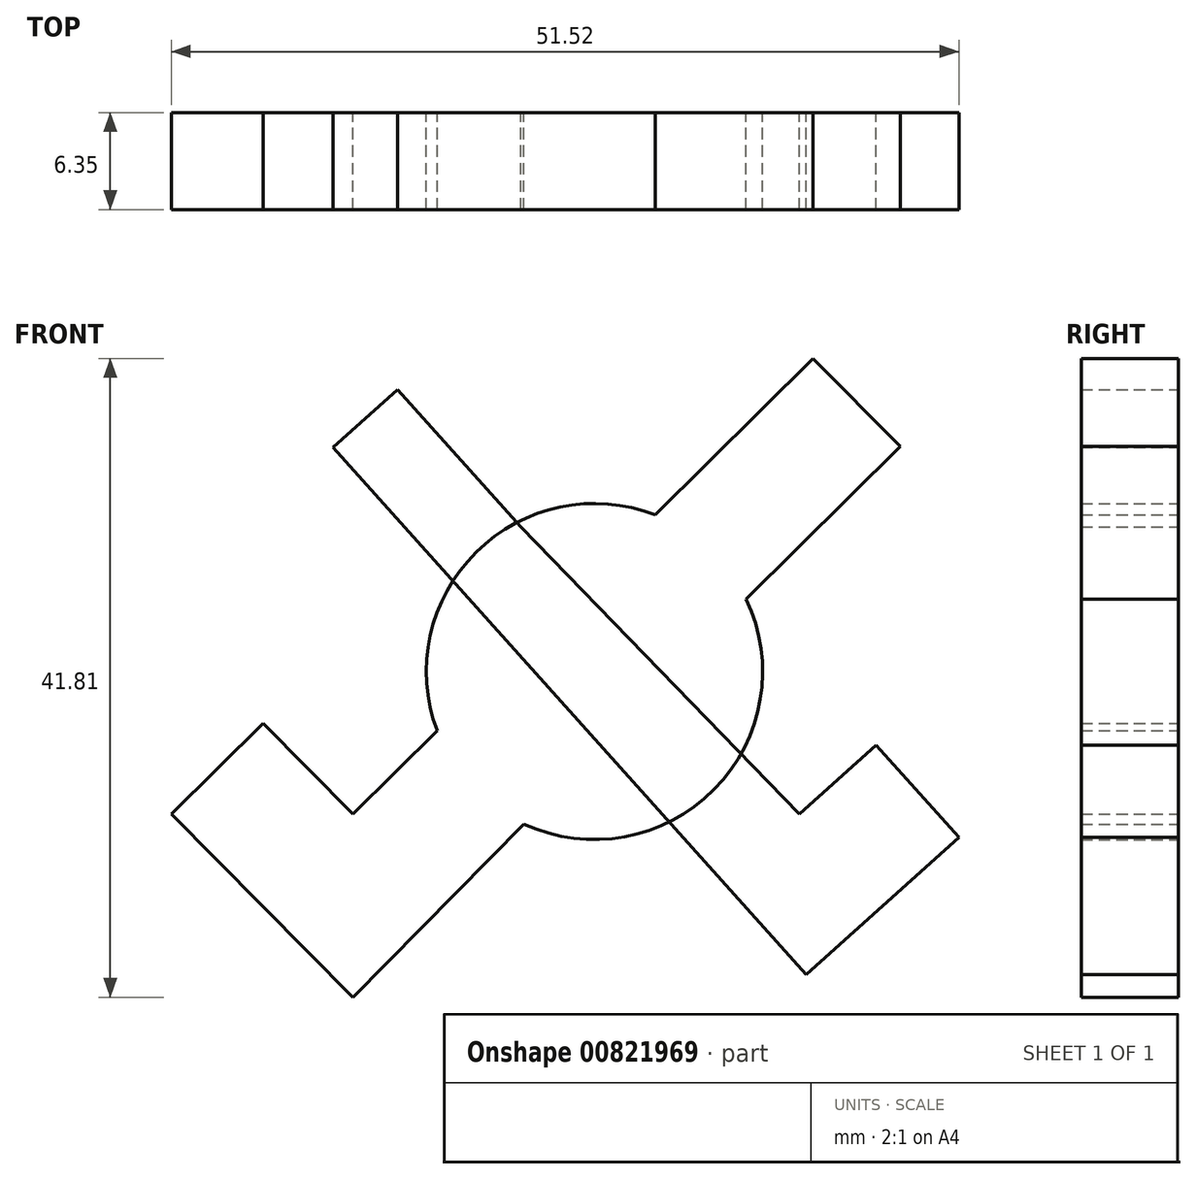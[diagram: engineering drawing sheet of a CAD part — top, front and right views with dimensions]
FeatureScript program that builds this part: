
annotation { "Feature Type Name" : "Feature", "Feature Type Description" : "" }
export const myFeature = defineFeature(function(context is Context, id is Id, definition is map)
    precondition{}
    {
        {
            var Q0;
            Q0=qCreatedBy(makeId("Front.planeOp"),FACE);
            var sketch = newSketch(context, id + "F0", { "sketchPlane" : qUnion([Q0])});
            skCircle(sketch, "E0", {"center": v(0, 0) * mm, "radius": 11 * mm});
            skLineSegment(sketch, "E1", {"start": v(9.92, 4.74) * mm, "end": v(20, 14.73) * mm});
            skLineSegment(sketch, "E2", {"start": v(20, 14.73) * mm, "end": v(14.3, 20.49) * mm});
            skLineSegment(sketch, "E3", {"start": v(14.3, 20.49) * mm, "end": v(-15.8, -9.33) * mm});
            skLineSegment(sketch, "E4", {"start": v(-15.8, -9.33) * mm, "end": v(-21.68, -3.4) * mm});
            skLineSegment(sketch, "E5", {"start": v(-21.68, -3.4) * mm, "end": v(-27.68, -9.33) * mm});
            skLineSegment(sketch, "E6", {"start": v(-27.68, -9.33) * mm, "end": v(-15.8, -21.32) * mm});
            skLineSegment(sketch, "E7", {"start": v(-15.8, -21.32) * mm, "end": v(9.92, 4.74) * mm});
            skSolve(sketch);
        }
        {
            var Q0;
            Q0=qCreatedBy(makeId("Front.planeOp"),FACE);
            var sketch = newSketch(context, id + "F1", { "sketchPlane" : qUnion([Q0])});
            skLineSegment(sketch, "E8", {"start": v(-4.8, 9.46) * mm, "end": v(-12.87, 18.45) * mm});
            skLineSegment(sketch, "E9", {"start": v(-12.87, 18.45) * mm, "end": v(-17.1, 14.67) * mm});
            skLineSegment(sketch, "E10", {"start": v(-17.1, 14.67) * mm, "end": v(13.84, -19.84) * mm});
            skLineSegment(sketch, "E11", {"start": v(13.84, -19.84) * mm, "end": v(23.84, -10.87) * mm});
            skLineSegment(sketch, "E12", {"start": v(23.84, -10.87) * mm, "end": v(18.43, -4.83) * mm});
            skLineSegment(sketch, "E13", {"start": v(18.43, -4.83) * mm, "end": v(13.4, -9.33) * mm});
            skLineSegment(sketch, "E14", {"start": v(13.4, -9.33) * mm, "end": v(-4.8, 9.46) * mm});
            skSolve(sketch);
        }
        {
            var Q0;
            Q0=makeQuery(id+"F1.imprint","IMPRINT",FACE,{"disambiguationData":[TD([[makeQuery(id+"F1.imprint","IMPRINT",EDGE,{"derivedFrom":sQuery(id+"F1.wireOp",EDGE,"E8")}),1.0]])]});
            var Q1;
            {var subQ0=sQuery(id+"F0.wireOp",EDGE,"E4");Q1=makeQuery(id+"F0.imprint","IMPRINT",FACE,{"disambiguationData":[TD([[makeQuery(id+"F0.imprint","IMPRINT",EDGE,{"derivedFrom":subQ0}),1.0]])]});}
            var Q2;
            {var subQ0=sQuery(id+"F0.wireOp",EDGE,"E1");Q2=makeQuery(id+"F0.imprint","IMPRINT",FACE,{"disambiguationData":[TD([[makeQuery(id+"F0.imprint","IMPRINT",EDGE,{"derivedFrom":subQ0}),1.0]])]});}
            var Q3;
            {var subQ0=sQuery(id+"F0.wireOp",EDGE,"E3");var subQ1=sQuery(id+"F0.wireOp",EDGE,"E0");var subQ2=makeQuery(id+"F0.imprint","INTERSECT",VERTEX,{"disambiguationData":[OD(0.0)],"derivedFrom":[subQ1,subQ0]});Q3=makeQuery(id+"F0.imprint","IMPRINT",FACE,{"disambiguationData":[TD([[makeQuery(id+"F0.imprint","IMPRINT",EDGE,{"disambiguationData":[TD([[subQ2,-1.0]])],"derivedFrom":subQ1}),1.0]])]});}
            var Q4;
            {var subQ0=sQuery(id+"F0.wireOp",EDGE,"E7");var subQ1=sQuery(id+"F0.wireOp",EDGE,"E0");var subQ3=makeQuery(id+"F0.imprint","INTERSECT",VERTEX,{"derivedFrom":[subQ1,subQ0]});Q4=makeQuery(id+"F0.imprint","IMPRINT",FACE,{"disambiguationData":[TD([[makeQuery(id+"F0.imprint","IMPRINT",EDGE,{"disambiguationData":[TD([[subQ3,-1.0]])],"derivedFrom":subQ1}),1.0]])]});}
            var Q5;
            {var subQ1=sQuery(id+"F0.wireOp",EDGE,"E0");var subQ3=sQuery(id+"F0.wireOp",EDGE,"E3");var subQ5=makeQuery(id+"F0.imprint","INTERSECT",VERTEX,{"disambiguationData":[OD(1.0)],"derivedFrom":[subQ1,subQ3]});Q5=makeQuery(id+"F0.imprint","IMPRINT",FACE,{"disambiguationData":[TD([[makeQuery(id+"F0.imprint","IMPRINT",EDGE,{"disambiguationData":[TD([[subQ5,-1.0]])],"derivedFrom":subQ1}),1.0]])]});}
            extrude(context, id + "F2", {"entities" : qUnion([Q0, Q1, Q2, Q3, Q4, Q5]), "depth" : 6.35 * mm, "offsetDistance" : 25.4 * mm});
        }
    });
